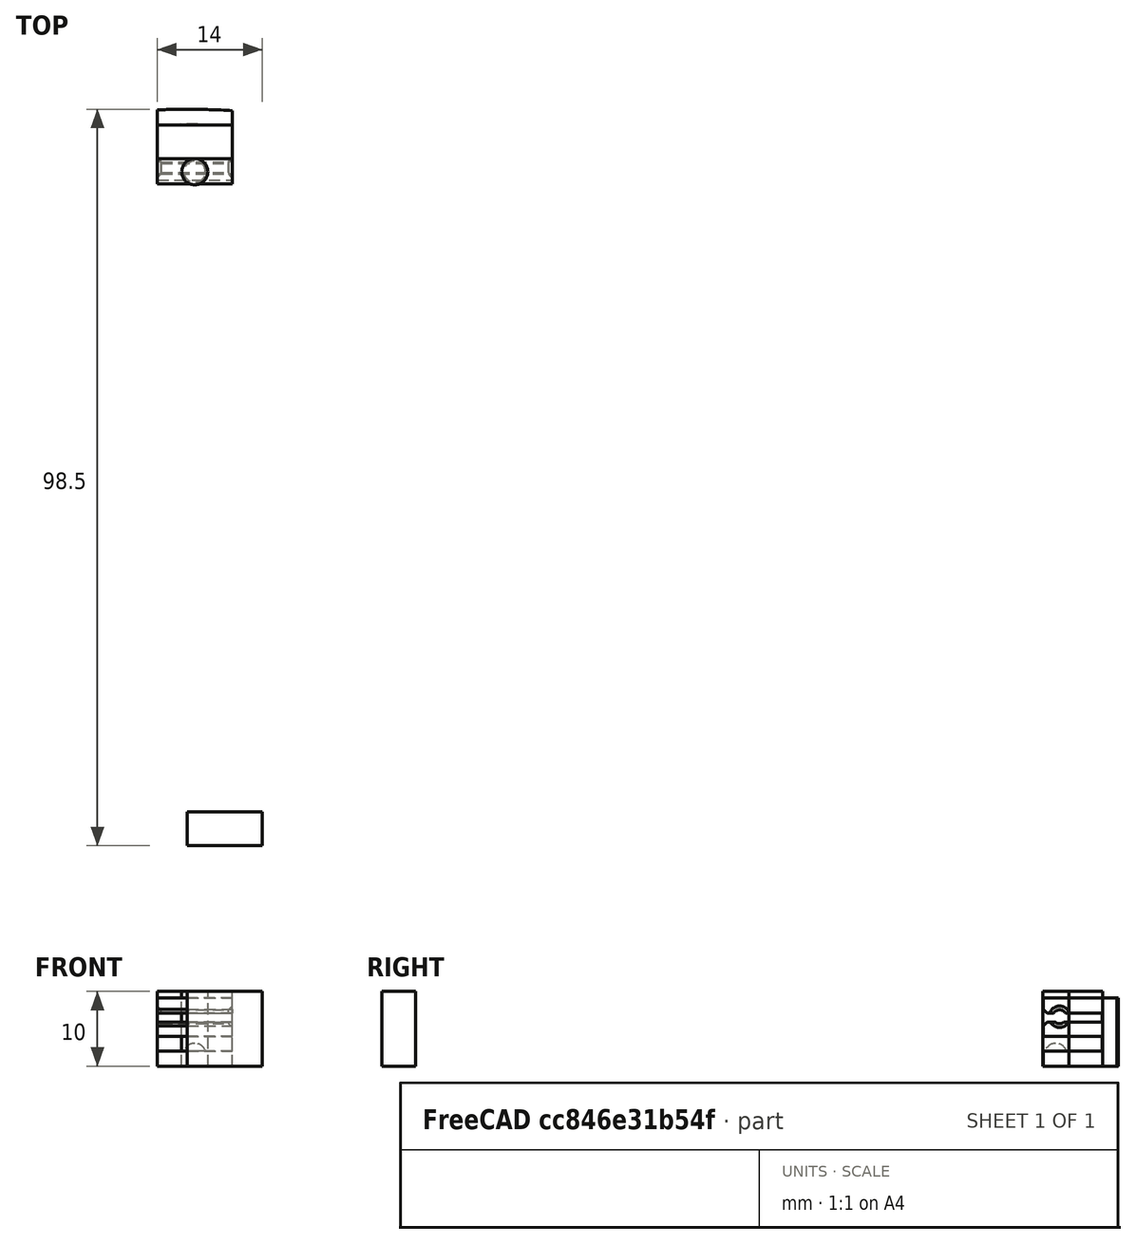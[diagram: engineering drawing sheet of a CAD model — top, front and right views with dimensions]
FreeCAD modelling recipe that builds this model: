
FCSTD DOCUMENT  (FreeCAD 0.18R14555 (Git shallow))
Label: creality-spool-clip
License: All rights reserved
LicenseURL: http://en.wikipedia.org/wiki/All_rights_reserved
objects: Part::Cylinder×5, Part::Box×4, Part::Cut×4, Part::Chamfer×2, Part::Feature×2, Part::MultiCommon×1, Part::Sphere×1, Part::MultiFuse×1
note: 20 computed .brp shape members not serialized (recipe doc carries the construction recipe); baked Part::Feature solids carry a one-line shape summary decoded from their .brp

FEATURE [Part::Cylinder] Cylinder
  Angle = 360
  AttacherType = Attacher::AttachEngine3D
  Height = 1.2
  Placement = pos=(0,0,5.9) rot=(0,0,1;0rad)
  Radius = 100
FEATURE [Part::Cylinder] Cylinder001
  Angle = 360
  AttacherType = Attacher::AttachEngine3D
  Height = 10
  Radius = 102
FEATURE [Part::Box] Box  label="Cube"
  AttacherType = Attacher::AttachEngine3D
  Height = 10
  Length = 10
  Placement = pos=(-4,92,0) rot=(0,0,1;0rad)
  Width = 10
FEATURE [Part::MultiCommon] Common
  Shapes = -> [Cylinder001,Box]
FEATURE [Part::Cylinder] Cylinder002
  Angle = 360
  AttacherType = Attacher::AttachEngine3D
  Height = 2
  Placement = pos=(0,0,2) rot=(0,0,1;0rad)
  Radius = 100
FEATURE [Part::Cylinder] Cylinder003
  Angle = 360
  AttacherType = Attacher::AttachEngine3D
  Height = 21
  Placement = pos=(-6.38942,94.1591,6.6) rot=(0,-1,0;4.71239rad)
  Radius = 0.925
  expr: Radius = 1.85 / 2
FEATURE [Part::Box] Box002  label="Cube002"
  AttacherType = Attacher::AttachEngine3D
  Height = 10
  Length = 10
  Placement = pos=(0,3.5,0) rot=(0,0,1;0rad)
  Width = 4.5
FEATURE [Part::Cut] Cut
  Base = -> Common
  Tool = -> Cylinder002
FEATURE [Part::Cut] Cut001
  Base = -> Cut
  Tool = -> Cylinder
FEATURE [Part::Cut] Cut002
  Base = -> Cut001
  Tool = -> Cylinder003
FEATURE [Part::Box] Box003  label="Cube003"
  AttacherType = Attacher::AttachEngine3D
  Height = 10
  Length = 22
  Placement = pos=(-10.7,88.4,9.1) rot=(0,0,1;0rad)
  Width = 27
FEATURE [Part::Cut] Cut003
  Base = -> Cut002
  Tool = -> Box003
FEATURE [Part::Chamfer] Chamfer
  Base = -> Cut003
  Edges = 2 edges r=0.5: [Edge43,Edge47]
FEATURE [Part::Box] Box004  label="Cube004"
  AttacherType = Attacher::AttachEngine3D
  Height = 10
  Length = 10
  Placement = pos=(-4,95.4,0) rot=(0,0,1;0rad)
  Width = 4.5
FEATURE [Part::Chamfer] Chamfer001
  Base = -> Chamfer
  Edges = 6 edges r=0.5: [Edge6,Edge8,Edge16,Edge32,Edge35,Edge53]
FEATURE [Part::Cylinder] Cylinder004
  Angle = 360
  AttacherType = Attacher::AttachEngine3D
  Height = 10
  Placement = pos=(1,93.65,0) rot=(0,0,1;0rad)
  Radius = 1.75
  expr: Radius = 3.5 / 2
FEATURE [Part::Sphere] Sphere
  Angle1 = -90
  Angle2 = 90
  Angle3 = 360
  AttacherType = Attacher::AttachEngine3D
  Placement = pos=(1,93.65,1.55) rot=(0,0,1;0rad)
  Radius = 1.5
  expr: Radius = 1.5
FEATURE [Part::MultiFuse] Fusion
  Shapes = -> [Sphere,Chamfer001]
FEATURE [Part::Feature] Fusion001
  shape: bbox 10 x 10 x 9.1 mm, 27 faces (baked)
FEATURE [Part::Feature] Fusion001_solid  label="Fusion001 (Solid)"
  shape: bbox 10 x 10 x 9.1 mm, 27 faces (baked)
